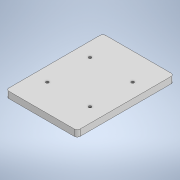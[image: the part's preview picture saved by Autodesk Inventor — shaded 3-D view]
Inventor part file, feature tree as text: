
AUTODESK INVENTOR PART (.ipt)
format: ipt  version: 2022 (Build 260153000, 153)  size: 149,504 bytes
history: native  units: mm
features: extrude x3, sketch x3, fillet x2
ambient origin geometry x8: Origin, YZ Plane, XZ Plane, XY Plane, X Axis, Y Axis, Z Axis, Center Point
bodies: Solid1 (feature_tree)
feature tree (8):
  extrude  "Extrusion1"  Depth=68.0mm
  extrude  "Extrusion2"  Depth=2.0mm
  extrude  "Extrusion3"  Depth=2.0mm
  fillet  "Fillet1"  Radius=2.0mm
  fillet  "Fillet2"  Radius=4.5mm
  sketch  "Sketch1"  dims[d0=50.0mm d1=68.0mm]
  sketch  "Sketch2"  dims[d2=4.5mm d3=0.0mm d4=2.0mm]
  sketch  "Sketch3"  dims[d5=2.0mm d6=2.0mm d7=2.0mm d8=4.5mm d9=0.0mm d10=5.0mm d11=5.0mm d12=5.0mm d13=5.0mm d14=0.0mm d15=2.0mm d16=1.0mm d17=0.0mm d18=0.0mm]
